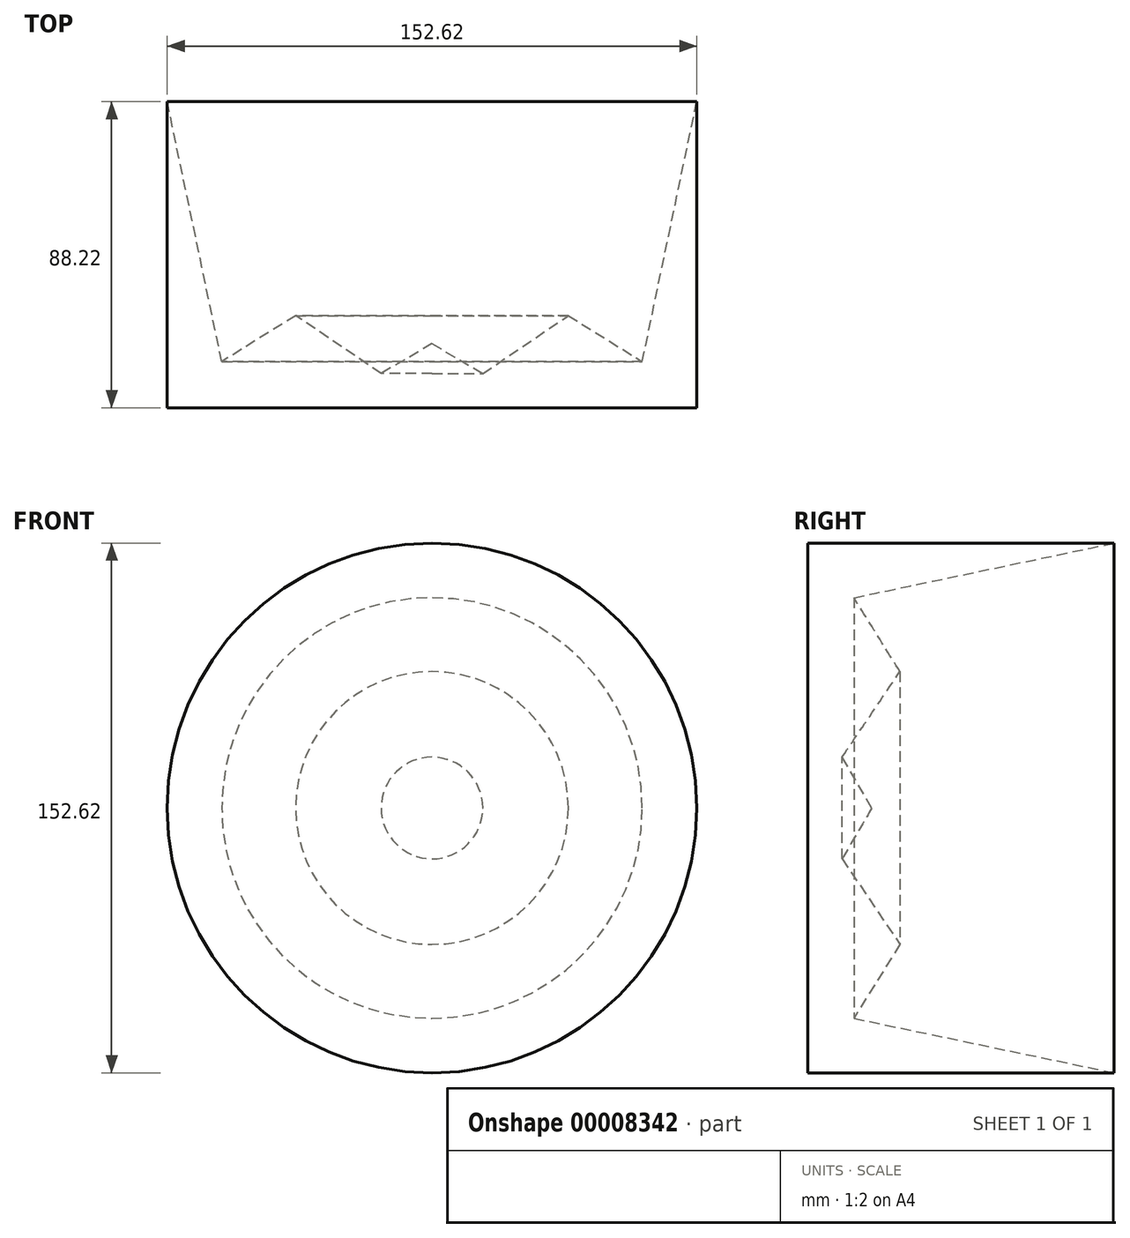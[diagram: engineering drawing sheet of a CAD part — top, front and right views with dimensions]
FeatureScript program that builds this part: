
annotation { "Feature Type Name" : "Feature", "Feature Type Description" : "" }
export const myFeature = defineFeature(function(context is Context, id is Id, definition is map)
    precondition{}
    {
        {
            var Q0;
            Q0=qCreatedBy(makeId("Top.planeOp"),FACE);
            var sketch = newSketch(context, id + "F0", { "sketchPlane" : qUnion([Q0])});
            skLineSegment(sketch, "E0", {"start": v(0, 0) * mm, "end": v(-76.31, 0) * mm});
            skLineSegment(sketch, "E1", {"start": v(-76.31, 0) * mm, "end": v(-76.31, 88.22) * mm});
            skLineSegment(sketch, "E2", {"start": v(-76.31, 88.22) * mm, "end": v(-60.59, 13.28) * mm});
            skLineSegment(sketch, "E3", {"start": v(-60.59, 13.28) * mm, "end": v(-39.3, 26.56) * mm});
            skLineSegment(sketch, "E4", {"start": v(-39.3, 26.56) * mm, "end": v(-14.65, 9.9) * mm});
            skLineSegment(sketch, "E5", {"start": v(-14.65, 9.9) * mm, "end": v(0, 18.46) * mm});
            skLineSegment(sketch, "E6", {"start": v(0, 18.46) * mm, "end": v(0, 0) * mm});
            skSolve(sketch);
        }
        {
            var Q0;
            Q0 = qSketchRegion(id + "F0", true);
            var Q1;
            Q1=sQuery(id+"F0.wireOp",EDGE,"E6");
            revolve(context, id + "F1", {"entities" : qUnion([Q0]), "axis" : qUnion([Q1]), "revolveType" : RevolveType.FULL});
        }
    });
